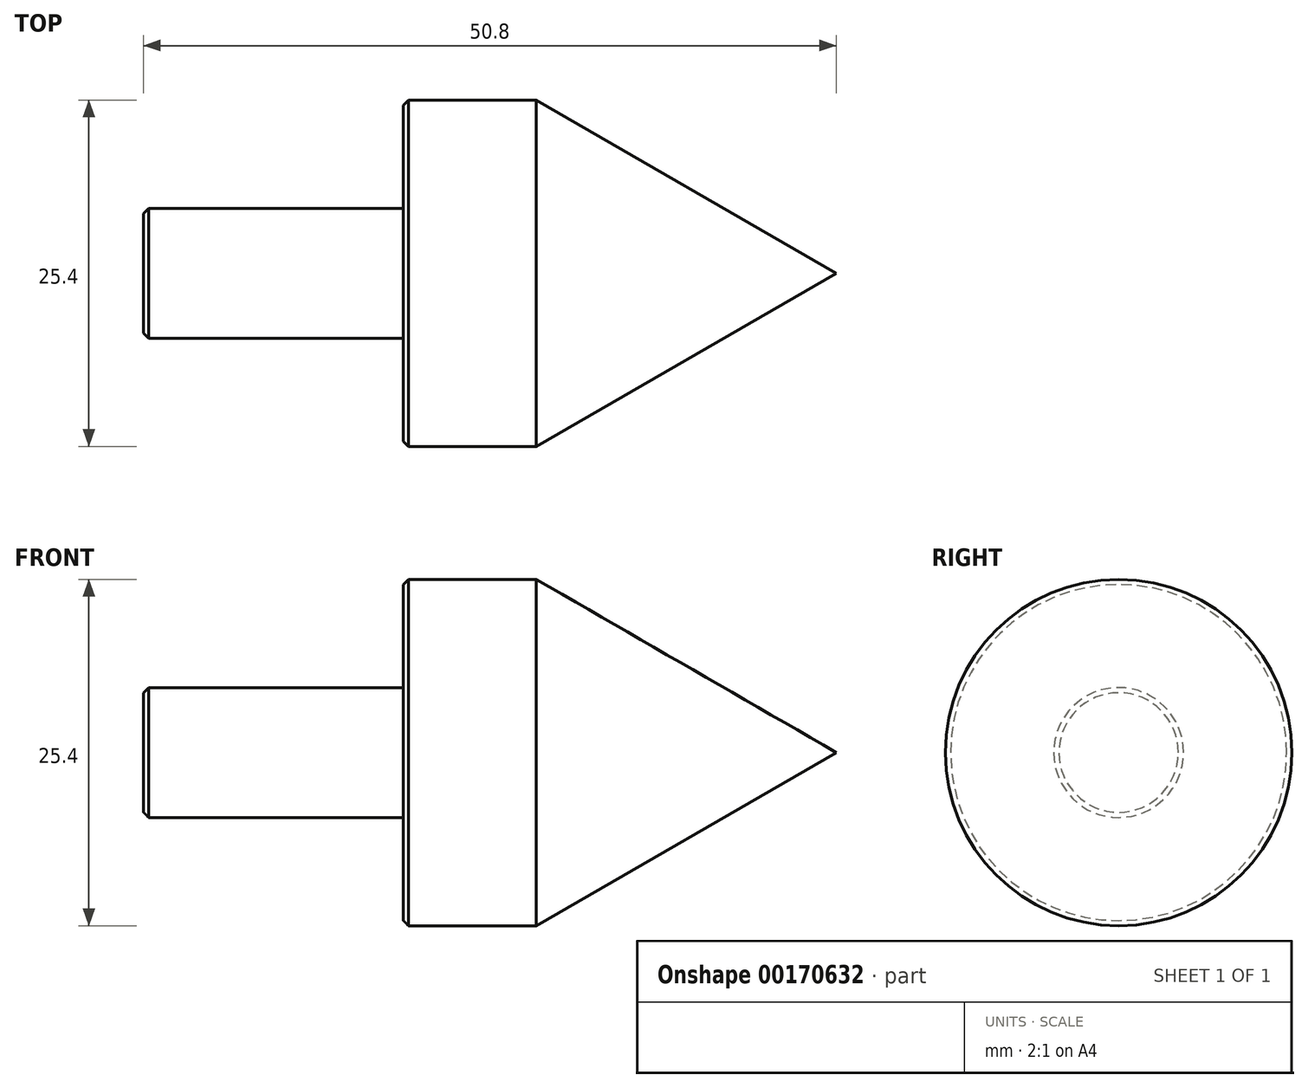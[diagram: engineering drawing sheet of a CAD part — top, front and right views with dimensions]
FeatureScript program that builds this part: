
annotation { "Feature Type Name" : "Feature", "Feature Type Description" : "" }
export const myFeature = defineFeature(function(context is Context, id is Id, definition is map)
    precondition{}
    {
        {
            var Q0;
            Q0=qCreatedBy(makeId("Top.planeOp"),FACE);
            var sketch = newSketch(context, id + "F0", { "sketchPlane" : qUnion([Q0])});
            skLineSegment(sketch, "E0", {"start": v(-31.9, 0) * mm, "end": v(-31.9, 4.76) * mm});
            skLineSegment(sketch, "E1", {"start": v(-31.9, 4.76) * mm, "end": v(-12.84, 4.76) * mm});
            skLineSegment(sketch, "E2", {"start": v(-12.84, 4.76) * mm, "end": v(-12.84, 12.7) * mm});
            skLineSegment(sketch, "E3", {"start": v(-12.84, 12.7) * mm, "end": v(-3.09, 12.7) * mm});
            skLineSegment(sketch, "E4", {"start": v(-3.09, 12.7) * mm, "end": v(18.9, 0) * mm});
            skLineSegment(sketch, "E5", {"start": v(18.9, 0) * mm, "end": v(-31.9, 0) * mm});
            skSolve(sketch);
        }
        {
            var Q0;
            Q0=makeQuery(id+"F0.imprint","IMPRINT",FACE,{"disambiguationData":[TD([[makeQuery(id+"F0.imprint","IMPRINT",EDGE,{"derivedFrom":sQuery(id+"F0.wireOp",EDGE,"E0")}),-1.0]])]});
            var Q1;
            Q1=sQuery(id+"F0.wireOp",EDGE,"E5");
            revolve(context, id + "F1", {"entities" : qUnion([Q0]), "axis" : qUnion([Q1]), "revolveType" : RevolveType.FULL});
        }
        {
            var Q0;
            Q0=makeQuery(id+"F1.opRevolve","SWEPT_EDGE",EDGE,{"disambiguationData":[OSD([sQuery(id+"F0.wireOp",EDGE,"E0"),sQuery(id+"F0.wireOp",EDGE,"E1")])]});
            var Q1;
            Q1=makeQuery(id+"F1.opRevolve","SWEPT_EDGE",EDGE,{"disambiguationData":[OSD([sQuery(id+"F0.wireOp",EDGE,"E2"),sQuery(id+"F0.wireOp",EDGE,"E3")])]});
            chamfer(context, id + "F2", {"entities" : qUnion([Q0, Q1]), "width" : 0.38 * mm, "tangentPropagation" : true});
        }
    });
